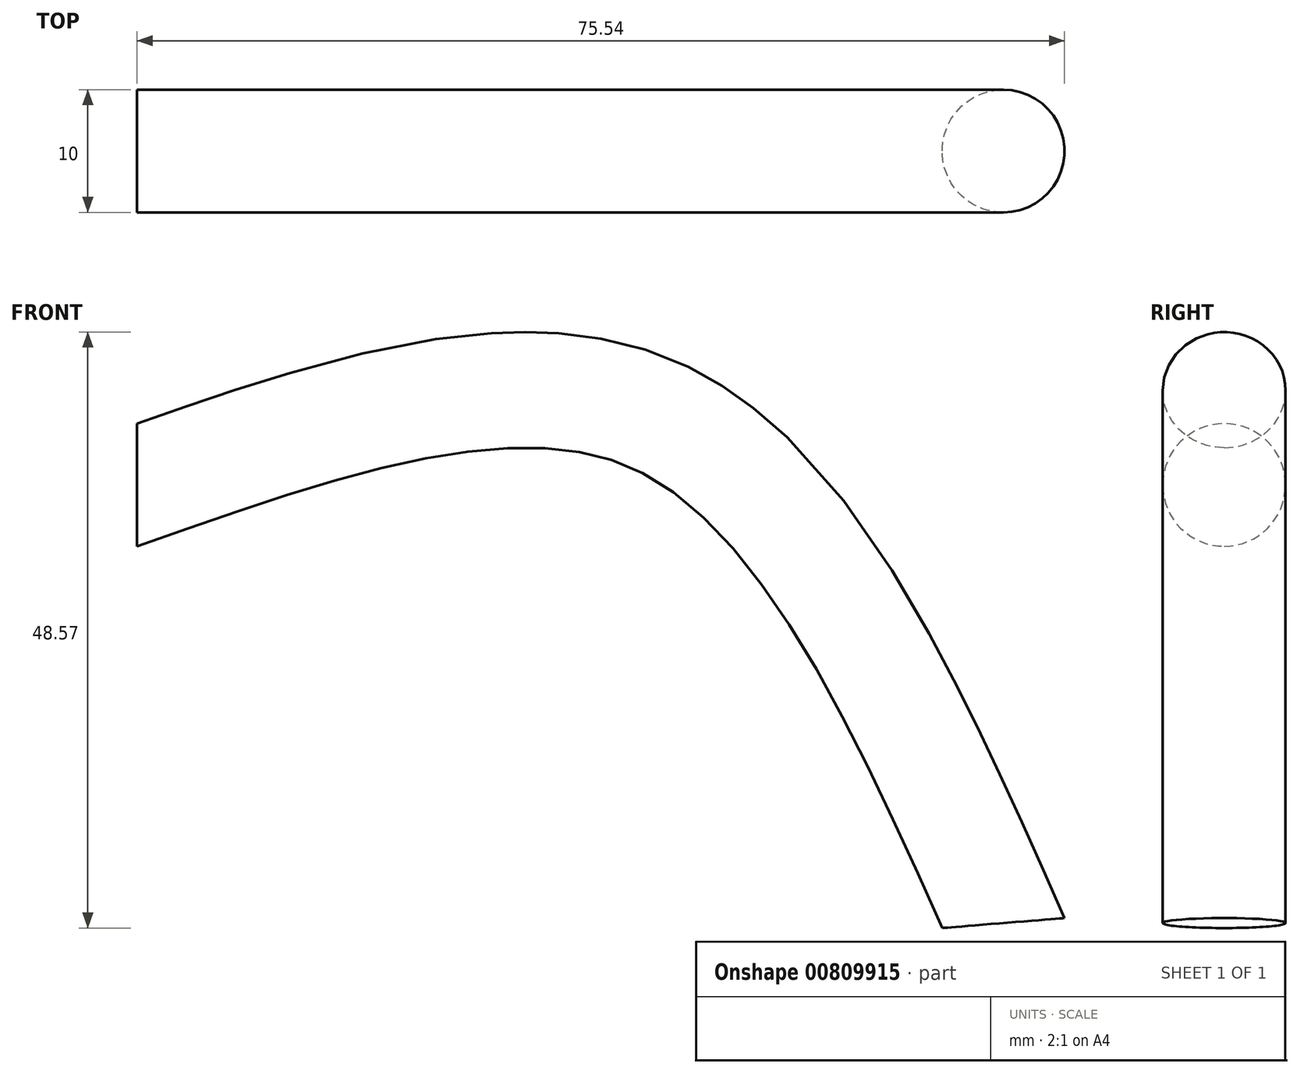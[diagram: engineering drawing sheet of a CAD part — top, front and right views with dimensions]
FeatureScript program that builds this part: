
annotation { "Feature Type Name" : "Feature", "Feature Type Description" : "" }
export const myFeature = defineFeature(function(context is Context, id is Id, definition is map)
    precondition{}
    {
        {
            var Q0;
            Q0=qCreatedBy(makeId("Front.planeOp"),FACE);
            var sketch = newSketch(context, id + "F0", { "sketchPlane" : qUnion([Q0])});
            skFitSpline(sketch, "E0", {"points": [v(0, 0) * mm, v(42.13, 5.66) * mm, v(70.56, -35.7) * mm], "startDerivative": vector(95.9, 33.67) * mm, "endDerivative": vector(45.92, -103.18) * mm});
            skSolve(sketch);
        }
        {
            var Q0;
            Q0=sQuery(id+"F0.wireOp",VERTEX,"E0.end");
            var Q1;
            Q1=sQuery(id+"F0.wireOp",EDGE,"E0");
            cPlane(context, id + "F1", {"entities" : qUnion([Q0, Q1]), "cplaneType" : CPlaneType.CURVE_POINT, "offset" : 25 * mm, "width" : 150 * mm, "height" : 150 * mm});
        }
        {
            var Q0;
            Q0=qCreatedBy(makeId("Right.planeOp"),FACE);
            var sketch = newSketch(context, id + "F2", { "sketchPlane" : qUnion([Q0])});
            skCircle(sketch, "E1", {"center": v(0, 0) * mm, "radius": 5 * mm});
            skSolve(sketch);
        }
        {
            var Q0;
            Q0=makeQuery(id+"F2.imprint","IMPRINT",FACE,{"disambiguationData":[TD([[makeQuery(id+"F2.imprint","IMPRINT",EDGE,{"derivedFrom":sQuery(id+"F2.wireOp",EDGE,"E1")}),1.0]])]});
            var Q1;
            Q1=sQuery(id+"F0.wireOp",EDGE,"E0");
            sweep(context, id + "F3", {"profiles" : qUnion([Q0]), "path" : qUnion([Q1])});
        }
    });
